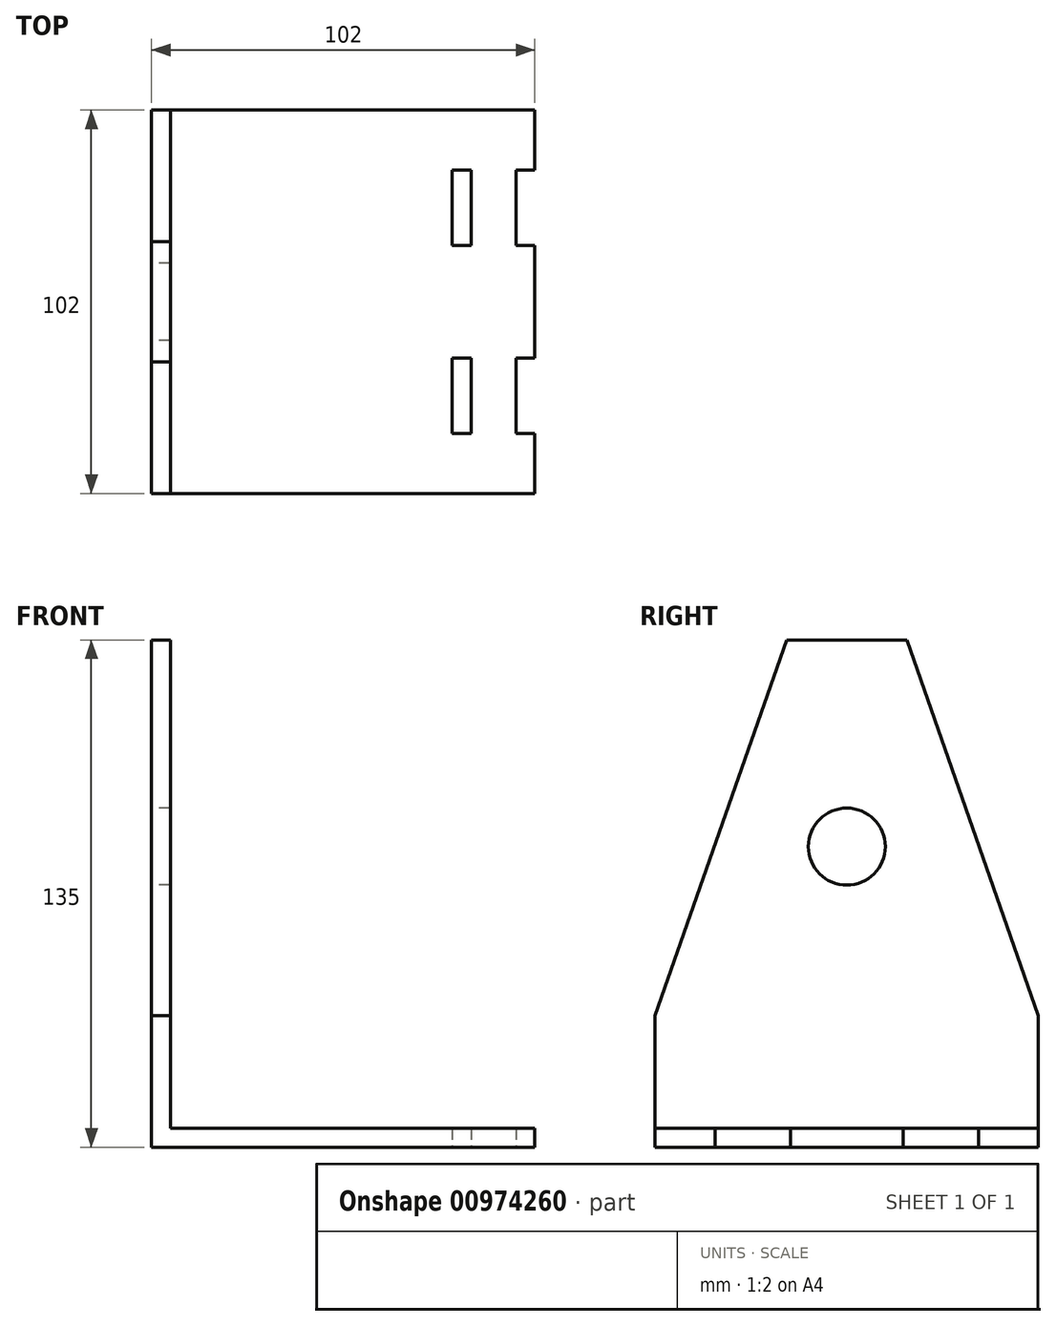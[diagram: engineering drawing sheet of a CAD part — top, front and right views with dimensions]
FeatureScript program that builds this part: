
annotation { "Feature Type Name" : "Feature", "Feature Type Description" : "" }
export const myFeature = defineFeature(function(context is Context, id is Id, definition is map)
    precondition{}
    {
        {
            var Q0;
            Q0=qCreatedBy(makeId("Top.planeOp"),FACE);
            var sketch = newSketch(context, id + "F0", { "sketchPlane" : qUnion([Q0])});
            skLineSegment(sketch, "E0.bottom", {"start": v(51, 51) * mm, "end": v(-51, 51) * mm});
            skLineSegment(sketch, "E0.top", {"start": v(51, -51) * mm, "end": v(-51, -51) * mm});
            skLineSegment(sketch, "E0.left", {"start": v(51, 51) * mm, "end": v(51, -51) * mm});
            skLineSegment(sketch, "E0.right", {"start": v(-51, 51) * mm, "end": v(-51, -51) * mm});
            skPoint(sketch, "E0.middle", {"position": v(0, 0) * mm});
            skLineSegment(sketch, "E1", {"start": v(-46, 51) * mm, "end": v(-46, -51) * mm});
            skLineSegment(sketch, "E2", {"start": v(29, 51) * mm, "end": v(29, -51) * mm});
            skLineSegment(sketch, "E3", {"start": v(34, 51) * mm, "end": v(34, -51) * mm});
            skLineSegment(sketch, "E4", {"start": v(46, 51) * mm, "end": v(46, -49) * mm});
            skLineSegment(sketch, "E5", {"start": v(34, 46) * mm, "end": v(46, 46) * mm, "construction": true});
            skLineSegment(sketch, "E6", {"start": v(34, -46) * mm, "end": v(46, -46) * mm, "construction": true});
            skLineSegment(sketch, "E7", {"start": v(51, 35) * mm, "end": v(29, 35) * mm});
            skLineSegment(sketch, "E8", {"start": v(29, 15) * mm, "end": v(51, 15) * mm});
            skLineSegment(sketch, "E9.MirrorCS", {"start": v(29, 55) * mm, "end": v(51, 55) * mm, "construction": true});
            skLineSegment(sketch, "E10.MirrorCS", {"start": v(29, -15) * mm, "end": v(51, -15) * mm});
            skLineSegment(sketch, "E11.MirrorCS", {"start": v(51, -35) * mm, "end": v(29, -35) * mm});
            skSolve(sketch);
        }
        {
            var Q0;
            {var subQ4=sQuery(id+"F0.wireOp",EDGE,"E1");Q0=makeQuery(id+"F0.imprint","IMPRINT",FACE,{"disambiguationData":[TD([[makeQuery(id+"F0.imprint","IMPRINT",EDGE,{"derivedFrom":subQ4}),1.0]])]});}
            var Q1;
            {var subQ0=sQuery(id+"F0.wireOp",EDGE,"E2");var subQ1=sQuery(id+"F0.wireOp",EDGE,"E0.bottom");var subQ2=makeQuery(id+"F0.imprint","INTERSECT",VERTEX,{"derivedFrom":[subQ1,subQ0]});Q1=makeQuery(id+"F0.imprint","IMPRINT",FACE,{"disambiguationData":[TD([[makeQuery(id+"F0.imprint","IMPRINT",EDGE,{"disambiguationData":[TD([[subQ2,1.0]])],"derivedFrom":subQ1}),1.0]])]});}
            var Q2;
            {var subQ0=sQuery(id+"F0.wireOp",EDGE,"E3");var subQ1=sQuery(id+"F0.wireOp",EDGE,"E0.bottom");var subQ2=makeQuery(id+"F0.imprint","INTERSECT",VERTEX,{"derivedFrom":[subQ1,subQ0]});Q2=makeQuery(id+"F0.imprint","IMPRINT",FACE,{"disambiguationData":[TD([[makeQuery(id+"F0.imprint","IMPRINT",EDGE,{"disambiguationData":[TD([[subQ2,1.0]])],"derivedFrom":subQ1}),1.0]])]});}
            var Q3;
            {var subQ0=sQuery(id+"F0.wireOp",EDGE,"E8");var subQ1=sQuery(id+"F0.wireOp",EDGE,"E2");var subQ2=makeQuery(id+"F0.imprint","INTERSECT",VERTEX,{"derivedFrom":[subQ1,subQ0]});Q3=makeQuery(id+"F0.imprint","IMPRINT",FACE,{"disambiguationData":[TD([[makeQuery(id+"F0.imprint","IMPRINT",EDGE,{"disambiguationData":[TD([[subQ2,-1.0]])],"derivedFrom":subQ1}),1.0]])]});}
            var Q4;
            {var subQ0=sQuery(id+"F0.wireOp",EDGE,"E8");var subQ1=sQuery(id+"F0.wireOp",EDGE,"E3");var subQ2=makeQuery(id+"F0.imprint","INTERSECT",VERTEX,{"derivedFrom":[subQ1,subQ0]});Q4=makeQuery(id+"F0.imprint","IMPRINT",FACE,{"disambiguationData":[TD([[makeQuery(id+"F0.imprint","IMPRINT",EDGE,{"disambiguationData":[TD([[subQ2,-1.0]])],"derivedFrom":subQ1}),1.0]])]});}
            var Q5;
            {var subQ0=sQuery(id+"F0.wireOp",EDGE,"E2");var subQ1=sQuery(id+"F0.wireOp",EDGE,"E0.top");var subQ2=makeQuery(id+"F0.imprint","INTERSECT",VERTEX,{"derivedFrom":[subQ1,subQ0]});Q5=makeQuery(id+"F0.imprint","IMPRINT",FACE,{"disambiguationData":[TD([[makeQuery(id+"F0.imprint","IMPRINT",EDGE,{"disambiguationData":[TD([[subQ2,1.0]])],"derivedFrom":subQ1}),-1.0]])]});}
            var Q6;
            {var subQ0=sQuery(id+"F0.wireOp",EDGE,"E10.MirrorCS");var subQ1=sQuery(id+"F0.wireOp",EDGE,"E3");var subQ2=makeQuery(id+"F0.imprint","INTERSECT",VERTEX,{"derivedFrom":[subQ1,subQ0]});Q6=makeQuery(id+"F0.imprint","IMPRINT",FACE,{"disambiguationData":[TD([[makeQuery(id+"F0.imprint","IMPRINT",EDGE,{"disambiguationData":[TD([[subQ2,-1.0]])],"derivedFrom":subQ1}),1.0]])]});}
            var Q7;
            {var subQ0=sQuery(id+"F0.wireOp",EDGE,"E7");var subQ1=sQuery(id+"F0.wireOp",EDGE,"E3");var subQ2=makeQuery(id+"F0.imprint","INTERSECT",VERTEX,{"derivedFrom":[subQ1,subQ0]});Q7=makeQuery(id+"F0.imprint","IMPRINT",FACE,{"disambiguationData":[TD([[makeQuery(id+"F0.imprint","IMPRINT",EDGE,{"disambiguationData":[TD([[subQ2,-1.0]])],"derivedFrom":subQ1}),1.0]])]});}
            var Q8;
            {var subQ1=sQuery(id+"F0.wireOp",EDGE,"E0.left");var subQ4=sQuery(id+"F0.wireOp",EDGE,"E0.top");var subQ5=makeQuery(id+"F0.imprint","INTERSECT",VERTEX,{"derivedFrom":[subQ4,subQ1]});Q8=makeQuery(id+"F0.imprint","IMPRINT",FACE,{"disambiguationData":[TD([[makeQuery(id+"F0.imprint","IMPRINT",EDGE,{"disambiguationData":[TD([[subQ5,-1.0]])],"derivedFrom":subQ4}),-1.0]])]});}
            var Q9;
            {var subQ0=sQuery(id+"F0.wireOp",EDGE,"E0.left");var subQ1=sQuery(id+"F0.wireOp",EDGE,"E0.bottom");var subQ2=makeQuery(id+"F0.imprint","INTERSECT",VERTEX,{"derivedFrom":[subQ1,subQ0]});Q9=makeQuery(id+"F0.imprint","IMPRINT",FACE,{"disambiguationData":[TD([[makeQuery(id+"F0.imprint","IMPRINT",EDGE,{"disambiguationData":[TD([[subQ2,-1.0]])],"derivedFrom":subQ1}),1.0]])]});}
            var Q10;
            {var subQ0=sQuery(id+"F0.wireOp",EDGE,"E8");var subQ1=sQuery(id+"F0.wireOp",EDGE,"E0.left");var subQ2=makeQuery(id+"F0.imprint","INTERSECT",VERTEX,{"derivedFrom":[subQ1,subQ0]});Q10=makeQuery(id+"F0.imprint","IMPRINT",FACE,{"disambiguationData":[TD([[makeQuery(id+"F0.imprint","IMPRINT",EDGE,{"disambiguationData":[TD([[subQ2,-1.0]])],"derivedFrom":subQ1}),-1.0]])]});}
            extrude(context, id + "F1", {"entities" : qUnion([Q0, Q1, Q2, Q3, Q4, Q5, Q6, Q7, Q8, Q9, Q10]), "depth" : 5 * mm, "offsetDistance" : 25 * mm});
        }
        {
            var Q0;
            {var subQ0=sQuery(id+"F0.wireOp",EDGE,"E0.right");Q0=makeQuery(id+"F0.imprint","IMPRINT",FACE,{"disambiguationData":[TD([[makeQuery(id+"F0.imprint","IMPRINT",EDGE,{"derivedFrom":subQ0}),1.0]])]});}
            extrude(context, id + "F2", {"entities" : qUnion([Q0]), "operationType" : NewBodyOperationType.ADD, "depth" : 135 * mm, "offsetDistance" : 25 * mm});
        }
        {
            var Q0;
            Q0=makeQuery(id+"F2.opExtrude","CAP_EDGE",EDGE,{"disambiguationData":[OSD([sQuery(id+"F0.wireOp",EDGE,"E0.top")])],"isStart":false});
            var Q1;
            Q1=makeQuery(id+"F2.opExtrude","CAP_EDGE",EDGE,{"disambiguationData":[OSD([sQuery(id+"F0.wireOp",EDGE,"E0.bottom")])],"isStart":false});
            chamfer(context, id + "F3", {"entities" : qUnion([Q0, Q1]), "chamferType" : ChamferType.TWO_OFFSETS, "width1" : 100 * mm, "oppositeDirection" : false, "width2" : 35 * mm, "tangentPropagation" : true});
        }
        {
            var Q0;
            Q0=makeQuery(id+"F2.opExtrude","SWEPT_FACE",FACE,{"disambiguationData":[OSD([sQuery(id+"F0.wireOp",EDGE,"E0.right")])]});
            var sketch = newSketch(context, id + "F4", { "sketchPlane" : qUnion([Q0])});
            skLineSegment(sketch, "E12", {"start": v(0, 135) * mm, "end": v(0, 0) * mm, "construction": true});
            skLineSegment(sketch, "E13", {"start": v(-51, 5) * mm, "end": v(51, 5) * mm, "construction": true});
            skLineSegment(sketch, "E14", {"start": v(-51, 80) * mm, "end": v(51, 80) * mm, "construction": true});
            skPoint(sketch, "E15", {"position": v(0, 80) * mm});
            skSolve(sketch);
        }
        {
            var Q0;
            Q0=sQuery(id+"F4.wireOp",VERTEX,"E15");
            var Q1;
            Q1=makeQuery(id+"F1.opExtrude","SWEPT_BODY",BODY,{"disambiguationData":[OSD([sQuery(id+"F0.wireOp",EDGE,"E0.bottom"),sQuery(id+"F0.wireOp",EDGE,"E0.top"),sQuery(id+"F0.wireOp",EDGE,"E0.left"),sQuery(id+"F0.wireOp",EDGE,"E1")])]});
            hole(context, id + "F5", {"style" : HoleStyle.SIMPLE, "endStyle" : HoleEndStyle.THROUGH, "holeDiameter" : 20.5 * mm, "majorDiameter" : 5 * mm, "isTappedThrough" : true, "tappedDepth" : 12 * mm, "tapClearance" : 3, "locations" : qUnion([Q0]), "scope" : qUnion([Q1])});
        }
    });
